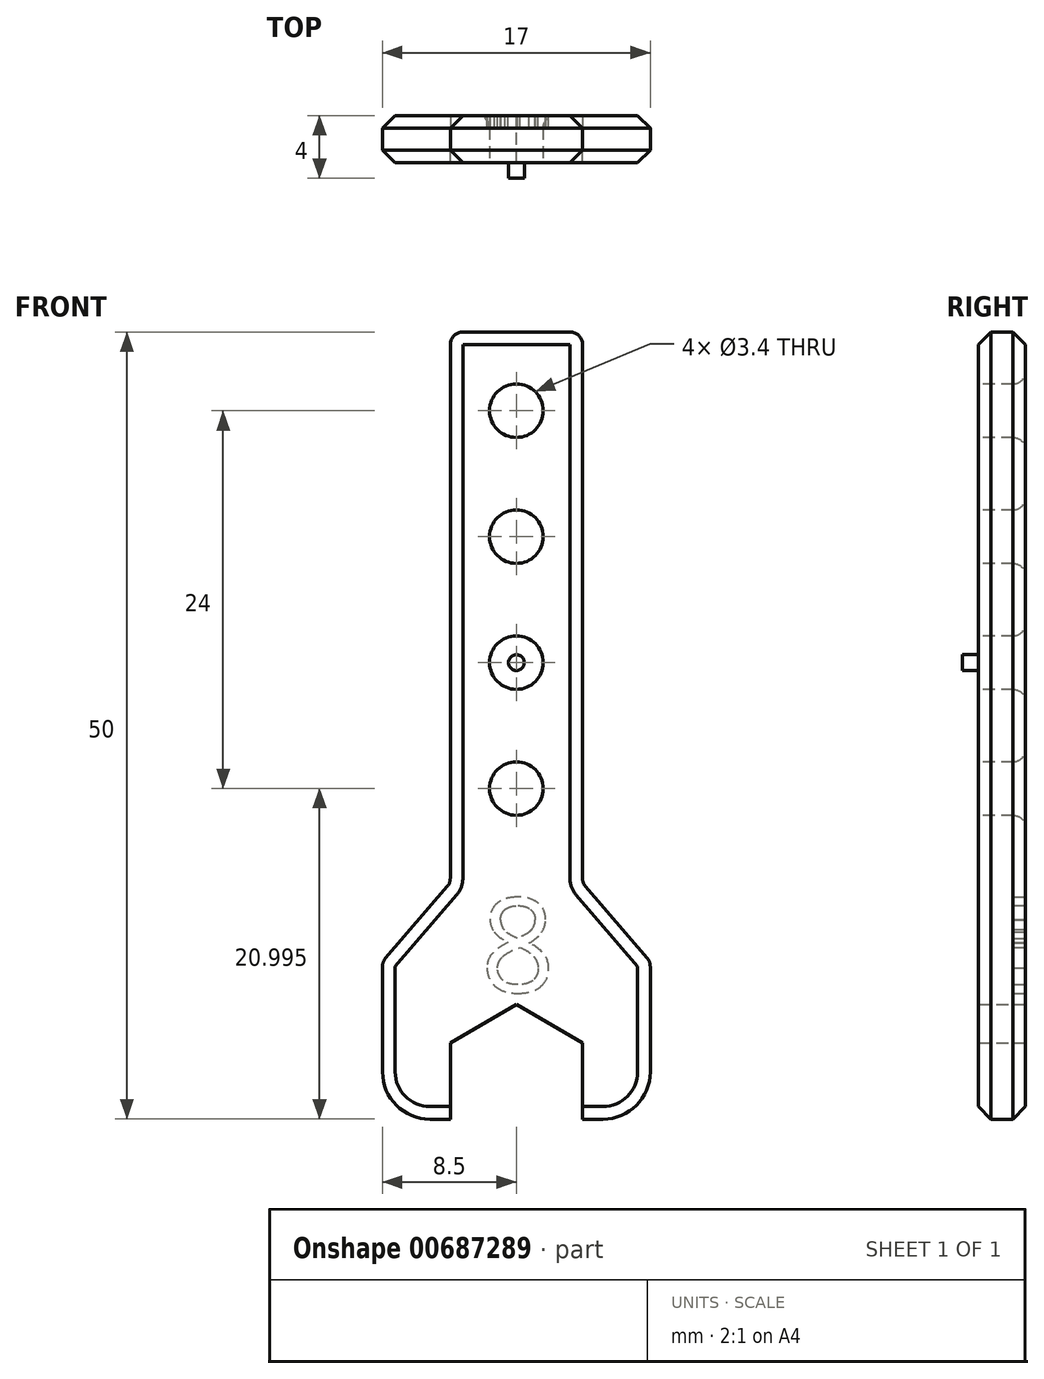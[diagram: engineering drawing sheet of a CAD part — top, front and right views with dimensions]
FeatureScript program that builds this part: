
annotation { "Feature Type Name" : "Feature", "Feature Type Description" : "" }
export const myFeature = defineFeature(function(context is Context, id is Id, definition is map)
    precondition{}
    {
        {
            var Q0;
            Q0=qCreatedBy(makeId("Front.planeOp"),FACE);
            var sketch = newSketch(context, id + "F0", { "sketchPlane" : qUnion([Q0])});
            skLineSegment(sketch, "E0.0", {"start": v(4.2, 2.42) * mm, "end": v(4.2, -2.42) * mm});
            skLineSegment(sketch, "E0.3", {"start": v(-4.2, -2.42) * mm, "end": v(-4.2, 2.42) * mm});
            skLineSegment(sketch, "E0.4", {"start": v(-4.2, 2.42) * mm, "end": v(0, 4.85) * mm});
            skLineSegment(sketch, "E0.5", {"start": v(0, 4.85) * mm, "end": v(2.1, 3.64) * mm});
            skPoint(sketch, "E0.0.midPoint", {"position": v(4.2, 0) * mm});
            skLineSegment(sketch, "E1", {"start": v(-8.5, -2.42) * mm, "end": v(-4.2, -2.42) * mm});
            skLineSegment(sketch, "E2", {"start": v(-8.5, -2.42) * mm, "end": v(-8.5, 7.58) * mm});
            skLineSegment(sketch, "E3", {"start": v(-8.5, 7.58) * mm, "end": v(-4.2, 12.58) * mm});
            skLineSegment(sketch, "E4", {"start": v(-4.2, 12.58) * mm, "end": v(-4.2, 47.58) * mm});
            skLineSegment(sketch, "E5", {"start": v(-4.2, 47.58) * mm, "end": v(0, 47.58) * mm});
            skLineSegment(sketch, "E6.MirrorCS", {"start": v(8.5, -2.42) * mm, "end": v(4.2, -2.42) * mm});
            skLineSegment(sketch, "E7.MirrorCS", {"start": v(4.2, 2.42) * mm, "end": v(0, 4.85) * mm});
            skLineSegment(sketch, "E8.MirrorCS", {"start": v(4.2, -2.42) * mm, "end": v(4.2, 2.42) * mm});
            skLineSegment(sketch, "E9.MirrorCS", {"start": v(4.2, 47.58) * mm, "end": v(0, 47.58) * mm});
            skLineSegment(sketch, "E10.MirrorCS", {"start": v(8.5, 7.58) * mm, "end": v(4.2, 12.58) * mm});
            skLineSegment(sketch, "E11.MirrorCS", {"start": v(8.5, -2.42) * mm, "end": v(8.5, 7.58) * mm});
            skLineSegment(sketch, "E12.MirrorCS", {"start": v(4.2, 12.58) * mm, "end": v(4.2, 47.58) * mm});
            skPoint(sketch, "E0.1.end.orphan", {"position": v(0, -4.85) * mm});
            skPoint(sketch, "E0.cCircle.center.orphan", {"position": v(0, 0) * mm});
            skSolve(sketch);
        }
        {
            var Q0;
            Q0=makeQuery(id+"F0.imprint","IMPRINT",FACE,{"disambiguationData":[TD([[makeQuery(id+"F0.imprint","IMPRINT",EDGE,{"derivedFrom":sQuery(id+"F0.wireOp",EDGE,"E0.3")}),1.0]])]});
            extrude(context, id + "F1", {"entities" : qUnion([Q0]), "endBound" : BoundingType.SYMMETRIC, "depth" : 3 * mm, "offsetDistance" : 25 * mm});
        }
        {
            var Q0;
            Q0=makeQuery(id+"F1.opExtrude","CAP_FACE",FACE,{"disambiguationData":[OSD([sQuery(id+"F0.wireOp",EDGE,"E0.3"),sQuery(id+"F0.wireOp",EDGE,"E0.4"),sQuery(id+"F0.wireOp",EDGE,"E1"),sQuery(id+"F0.wireOp",EDGE,"E2"),sQuery(id+"F0.wireOp",EDGE,"E3"),sQuery(id+"F0.wireOp",EDGE,"E4"),sQuery(id+"F0.wireOp",EDGE,"E5"),sQuery(id+"F0.wireOp",EDGE,"E6.MirrorCS"),sQuery(id+"F0.wireOp",EDGE,"E7.MirrorCS"),sQuery(id+"F0.wireOp",EDGE,"E8.MirrorCS"),sQuery(id+"F0.wireOp",EDGE,"E9.MirrorCS"),sQuery(id+"F0.wireOp",EDGE,"E10.MirrorCS"),sQuery(id+"F0.wireOp",EDGE,"E11.MirrorCS"),sQuery(id+"F0.wireOp",EDGE,"E12.MirrorCS")])],"isStart":false});
            var sketch = newSketch(context, id + "F2", { "sketchPlane" : qUnion([Q0])});
            skCircle(sketch, "E13", {"center": v(0, 42.58) * mm, "radius": 1.7 * mm});
            skCircle(sketch, "E14.0.1.0", {"center": v(0, 34.58) * mm, "radius": 1.7 * mm});
            skCircle(sketch, "E14.0.2.0", {"center": v(0, 26.58) * mm, "radius": 1.7 * mm});
            skCircle(sketch, "E14.0.3.0", {"center": v(0, 18.58) * mm, "radius": 1.7 * mm});
            skLineSegment(sketch, "E14.direction1", {"start": v(0, 42.58) * mm, "end": v(-27.7, 42.58) * mm, "construction": true});
            skLineSegment(sketch, "E14.direction2", {"start": v(0, 42.58) * mm, "end": v(0, 34.58) * mm, "construction": true});
            skSolve(sketch);
        }
        {
            var Q0;
            Q0 = qSketchRegion(id + "F2", true);
            extrude(context, id + "F3", {"entities" : qUnion([Q0]), "operationType" : NewBodyOperationType.REMOVE, "endBound" : BoundingType.THROUGH_ALL, "oppositeDirection" : true, "depth" : 25 * mm, "offsetDistance" : 25 * mm});
        }
        {
            var Q0;
            Q0=makeQuery(id+"F3.boolean.opBoolean","INTERSECT",EDGE,{"derivedFrom":[makeQuery(id+"F1.opExtrude","CAP_FACE",FACE,{"disambiguationData":[OSD([sQuery(id+"F0.wireOp",EDGE,"E0.3"),sQuery(id+"F0.wireOp",EDGE,"E0.4"),sQuery(id+"F0.wireOp",EDGE,"E1"),sQuery(id+"F0.wireOp",EDGE,"E2"),sQuery(id+"F0.wireOp",EDGE,"E3"),sQuery(id+"F0.wireOp",EDGE,"E4"),sQuery(id+"F0.wireOp",EDGE,"E5"),sQuery(id+"F0.wireOp",EDGE,"E6.MirrorCS"),sQuery(id+"F0.wireOp",EDGE,"E7.MirrorCS"),sQuery(id+"F0.wireOp",EDGE,"E8.MirrorCS"),sQuery(id+"F0.wireOp",EDGE,"E9.MirrorCS"),sQuery(id+"F0.wireOp",EDGE,"E10.MirrorCS"),sQuery(id+"F0.wireOp",EDGE,"E11.MirrorCS"),sQuery(id+"F0.wireOp",EDGE,"E12.MirrorCS")])],"isStart":true}),makeQuery(id+"F3.opExtrude","SWEPT_FACE",FACE,{"disambiguationData":[OSD([sQuery(id+"F2.wireOp",EDGE,"E14.0.4.0")])]})]});
            var Q1;
            Q1=makeQuery(id+"F3.boolean.opBoolean","INTERSECT",EDGE,{"derivedFrom":[makeQuery(id+"F1.opExtrude","CAP_FACE",FACE,{"disambiguationData":[OSD([sQuery(id+"F0.wireOp",EDGE,"E0.3"),sQuery(id+"F0.wireOp",EDGE,"E0.4"),sQuery(id+"F0.wireOp",EDGE,"E1"),sQuery(id+"F0.wireOp",EDGE,"E2"),sQuery(id+"F0.wireOp",EDGE,"E3"),sQuery(id+"F0.wireOp",EDGE,"E4"),sQuery(id+"F0.wireOp",EDGE,"E5"),sQuery(id+"F0.wireOp",EDGE,"E6.MirrorCS"),sQuery(id+"F0.wireOp",EDGE,"E7.MirrorCS"),sQuery(id+"F0.wireOp",EDGE,"E8.MirrorCS"),sQuery(id+"F0.wireOp",EDGE,"E9.MirrorCS"),sQuery(id+"F0.wireOp",EDGE,"E10.MirrorCS"),sQuery(id+"F0.wireOp",EDGE,"E11.MirrorCS"),sQuery(id+"F0.wireOp",EDGE,"E12.MirrorCS")])],"isStart":true}),makeQuery(id+"F3.opExtrude","SWEPT_FACE",FACE,{"disambiguationData":[OSD([sQuery(id+"F2.wireOp",EDGE,"E14.0.3.0")])]})]});
            var Q2;
            Q2=makeQuery(id+"F3.boolean.opBoolean","INTERSECT",EDGE,{"derivedFrom":[makeQuery(id+"F1.opExtrude","CAP_FACE",FACE,{"disambiguationData":[OSD([sQuery(id+"F0.wireOp",EDGE,"E0.3"),sQuery(id+"F0.wireOp",EDGE,"E0.4"),sQuery(id+"F0.wireOp",EDGE,"E1"),sQuery(id+"F0.wireOp",EDGE,"E2"),sQuery(id+"F0.wireOp",EDGE,"E3"),sQuery(id+"F0.wireOp",EDGE,"E4"),sQuery(id+"F0.wireOp",EDGE,"E5"),sQuery(id+"F0.wireOp",EDGE,"E6.MirrorCS"),sQuery(id+"F0.wireOp",EDGE,"E7.MirrorCS"),sQuery(id+"F0.wireOp",EDGE,"E8.MirrorCS"),sQuery(id+"F0.wireOp",EDGE,"E9.MirrorCS"),sQuery(id+"F0.wireOp",EDGE,"E10.MirrorCS"),sQuery(id+"F0.wireOp",EDGE,"E11.MirrorCS"),sQuery(id+"F0.wireOp",EDGE,"E12.MirrorCS")])],"isStart":true}),makeQuery(id+"F3.opExtrude","SWEPT_FACE",FACE,{"disambiguationData":[OSD([sQuery(id+"F2.wireOp",EDGE,"E13")])]})]});
            var Q3;
            Q3=makeQuery(id+"F3.boolean.opBoolean","INTERSECT",EDGE,{"derivedFrom":[makeQuery(id+"F1.opExtrude","CAP_FACE",FACE,{"disambiguationData":[OSD([sQuery(id+"F0.wireOp",EDGE,"E0.3"),sQuery(id+"F0.wireOp",EDGE,"E0.4"),sQuery(id+"F0.wireOp",EDGE,"E1"),sQuery(id+"F0.wireOp",EDGE,"E2"),sQuery(id+"F0.wireOp",EDGE,"E3"),sQuery(id+"F0.wireOp",EDGE,"E4"),sQuery(id+"F0.wireOp",EDGE,"E5"),sQuery(id+"F0.wireOp",EDGE,"E6.MirrorCS"),sQuery(id+"F0.wireOp",EDGE,"E7.MirrorCS"),sQuery(id+"F0.wireOp",EDGE,"E8.MirrorCS"),sQuery(id+"F0.wireOp",EDGE,"E9.MirrorCS"),sQuery(id+"F0.wireOp",EDGE,"E10.MirrorCS"),sQuery(id+"F0.wireOp",EDGE,"E11.MirrorCS"),sQuery(id+"F0.wireOp",EDGE,"E12.MirrorCS")])],"isStart":true}),makeQuery(id+"F3.opExtrude","SWEPT_FACE",FACE,{"disambiguationData":[OSD([sQuery(id+"F2.wireOp",EDGE,"E14.0.1.0")])]})]});
            var Q4;
            Q4=makeQuery(id+"F3.boolean.opBoolean","INTERSECT",EDGE,{"derivedFrom":[makeQuery(id+"F1.opExtrude","CAP_FACE",FACE,{"disambiguationData":[OSD([sQuery(id+"F0.wireOp",EDGE,"E0.3"),sQuery(id+"F0.wireOp",EDGE,"E0.4"),sQuery(id+"F0.wireOp",EDGE,"E1"),sQuery(id+"F0.wireOp",EDGE,"E2"),sQuery(id+"F0.wireOp",EDGE,"E3"),sQuery(id+"F0.wireOp",EDGE,"E4"),sQuery(id+"F0.wireOp",EDGE,"E5"),sQuery(id+"F0.wireOp",EDGE,"E6.MirrorCS"),sQuery(id+"F0.wireOp",EDGE,"E7.MirrorCS"),sQuery(id+"F0.wireOp",EDGE,"E8.MirrorCS"),sQuery(id+"F0.wireOp",EDGE,"E9.MirrorCS"),sQuery(id+"F0.wireOp",EDGE,"E10.MirrorCS"),sQuery(id+"F0.wireOp",EDGE,"E11.MirrorCS"),sQuery(id+"F0.wireOp",EDGE,"E12.MirrorCS")])],"isStart":true}),makeQuery(id+"F3.opExtrude","SWEPT_FACE",FACE,{"disambiguationData":[OSD([sQuery(id+"F2.wireOp",EDGE,"E14.0.2.0")])]})]});
            var Q5;
            Q5=makeQuery(id+"F3.boolean.opBoolean","COPY",EDGE,{"derivedFrom":makeQuery(id+"F3.opExtrude","CAP_EDGE",EDGE,{"disambiguationData":[OSD([sQuery(id+"F2.wireOp",EDGE,"E14.0.4.0")])],"isStart":true})});
            var Q6;
            Q6=makeQuery(id+"F3.boolean.opBoolean","COPY",EDGE,{"derivedFrom":makeQuery(id+"F3.opExtrude","CAP_EDGE",EDGE,{"disambiguationData":[OSD([sQuery(id+"F2.wireOp",EDGE,"E14.0.3.0")])],"isStart":true})});
            var Q7;
            Q7=makeQuery(id+"F3.boolean.opBoolean","COPY",EDGE,{"derivedFrom":makeQuery(id+"F3.opExtrude","CAP_EDGE",EDGE,{"disambiguationData":[OSD([sQuery(id+"F2.wireOp",EDGE,"E14.0.2.0")])],"isStart":true})});
            var Q8;
            Q8=makeQuery(id+"F3.boolean.opBoolean","COPY",EDGE,{"derivedFrom":makeQuery(id+"F3.opExtrude","CAP_EDGE",EDGE,{"disambiguationData":[OSD([sQuery(id+"F2.wireOp",EDGE,"E14.0.1.0")])],"isStart":true})});
            var Q9;
            Q9=makeQuery(id+"F3.boolean.opBoolean","COPY",EDGE,{"derivedFrom":makeQuery(id+"F3.opExtrude","CAP_EDGE",EDGE,{"disambiguationData":[OSD([sQuery(id+"F2.wireOp",EDGE,"E13")])],"isStart":true})});
            var Q10;
            Q10=makeQuery(id+"F1.opExtrude","SWEPT_EDGE",EDGE,{"disambiguationData":[OSD([sQuery(id+"F0.wireOp",EDGE,"E4"),sQuery(id+"F0.wireOp",EDGE,"E5")])]});
            var Q11;
            Q11=makeQuery(id+"F1.opExtrude","SWEPT_EDGE",EDGE,{"disambiguationData":[OSD([sQuery(id+"F0.wireOp",EDGE,"E9.MirrorCS"),sQuery(id+"F0.wireOp",EDGE,"E12.MirrorCS")])]});
            var Q12;
            Q12=makeQuery(id+"F1.opExtrude","SWEPT_EDGE",EDGE,{"disambiguationData":[OSD([sQuery(id+"F0.wireOp",EDGE,"E10.MirrorCS"),sQuery(id+"F0.wireOp",EDGE,"E11.MirrorCS")])]});
            var Q13;
            Q13=makeQuery(id+"F1.opExtrude","SWEPT_EDGE",EDGE,{"disambiguationData":[OSD([sQuery(id+"F0.wireOp",EDGE,"E3"),sQuery(id+"F0.wireOp",EDGE,"E4")])]});
            var Q14;
            Q14=makeQuery(id+"F1.opExtrude","SWEPT_EDGE",EDGE,{"disambiguationData":[OSD([sQuery(id+"F0.wireOp",EDGE,"E2"),sQuery(id+"F0.wireOp",EDGE,"E3")])]});
            var Q15;
            Q15=makeQuery(id+"F1.opExtrude","SWEPT_EDGE",EDGE,{"disambiguationData":[OSD([sQuery(id+"F0.wireOp",EDGE,"E10.MirrorCS"),sQuery(id+"F0.wireOp",EDGE,"E12.MirrorCS")])]});
            fillet(context, id + "F4", {"entities" : qUnion([Q0, Q1, Q2, Q3, Q4, Q5, Q6, Q7, Q8, Q9, Q10, Q11, Q12, Q13, Q14, Q15]), "radius" : 0.8 * mm, "tangentPropagation" : true, "allowEdgeOverflow" : false});
        }
        {
            var Q0;
            Q0=makeQuery(id+"F1.opExtrude","SWEPT_EDGE",EDGE,{"disambiguationData":[OSD([sQuery(id+"F0.wireOp",EDGE,"E1"),sQuery(id+"F0.wireOp",EDGE,"E2")])]});
            var Q1;
            Q1=makeQuery(id+"F1.opExtrude","SWEPT_EDGE",EDGE,{"disambiguationData":[OSD([sQuery(id+"F0.wireOp",EDGE,"E6.MirrorCS"),sQuery(id+"F0.wireOp",EDGE,"E11.MirrorCS")])]});
            fillet(context, id + "F5", {"entities" : qUnion([Q0, Q1]), "radius" : 3 * mm, "tangentPropagation" : true, "allowEdgeOverflow" : false});
        }
        {
            var Q0;
            Q0=makeQuery(id+"F1.opExtrude","CAP_EDGE",EDGE,{"disambiguationData":[OSD([sQuery(id+"F0.wireOp",EDGE,"E10.MirrorCS")])],"isStart":true});
            var Q1;
            Q1=makeQuery(id+"F1.opExtrude","CAP_EDGE",EDGE,{"disambiguationData":[OSD([sQuery(id+"F0.wireOp",EDGE,"E2")])],"isStart":false});
            chamfer(context, id + "F6", {"entities" : qUnion([Q0, Q1]), "width" : 0.8 * mm, "tangentPropagation" : true});
        }
        {
            var Q0;
            Q0=makeQuery(id+"F1.opExtrude","CAP_FACE",FACE,{"disambiguationData":[OSD([sQuery(id+"F0.wireOp",EDGE,"E0.3"),sQuery(id+"F0.wireOp",EDGE,"E0.4"),sQuery(id+"F0.wireOp",EDGE,"E1"),sQuery(id+"F0.wireOp",EDGE,"E2"),sQuery(id+"F0.wireOp",EDGE,"E3"),sQuery(id+"F0.wireOp",EDGE,"E4"),sQuery(id+"F0.wireOp",EDGE,"E5"),sQuery(id+"F0.wireOp",EDGE,"E6.MirrorCS"),sQuery(id+"F0.wireOp",EDGE,"E7.MirrorCS"),sQuery(id+"F0.wireOp",EDGE,"E8.MirrorCS"),sQuery(id+"F0.wireOp",EDGE,"E9.MirrorCS"),sQuery(id+"F0.wireOp",EDGE,"E10.MirrorCS"),sQuery(id+"F0.wireOp",EDGE,"E11.MirrorCS"),sQuery(id+"F0.wireOp",EDGE,"E12.MirrorCS")])],"isStart":true});
            var sketch = newSketch(context, id + "F7", { "sketchPlane" : qUnion([Q0])});
            skText(sketch, "E15", { "text": "8", "fontName": "OpenSans-Regular.ttf"});
            const initialGuessF7  = {"E15": [-0.00247, 0.00565, 1, 0, 0.006]};
            skSetInitialGuess(sketch, initialGuessF7);
            skSolve(sketch);
        }
        {
            var Q0;
            Q0 = qSketchRegion(id + "F7", true);
            extrude(context, id + "F8", {"entities" : qUnion([Q0]), "operationType" : NewBodyOperationType.REMOVE, "oppositeDirection" : true, "depth" : 0.8 * mm, "offsetDistance" : 25 * mm});
        }
        {
            var Q0;
            Q0=makeQuery(id+"F1.opExtrude","CAP_FACE",FACE,{"disambiguationData":[OSD([sQuery(id+"F0.wireOp",EDGE,"E0.3"),sQuery(id+"F0.wireOp",EDGE,"E0.4"),sQuery(id+"F0.wireOp",EDGE,"E1"),sQuery(id+"F0.wireOp",EDGE,"E2"),sQuery(id+"F0.wireOp",EDGE,"E3"),sQuery(id+"F0.wireOp",EDGE,"E4"),sQuery(id+"F0.wireOp",EDGE,"E5"),sQuery(id+"F0.wireOp",EDGE,"E6.MirrorCS"),sQuery(id+"F0.wireOp",EDGE,"E7.MirrorCS"),sQuery(id+"F0.wireOp",EDGE,"E8.MirrorCS"),sQuery(id+"F0.wireOp",EDGE,"E9.MirrorCS"),sQuery(id+"F0.wireOp",EDGE,"E10.MirrorCS"),sQuery(id+"F0.wireOp",EDGE,"E11.MirrorCS"),sQuery(id+"F0.wireOp",EDGE,"E12.MirrorCS")])],"isStart":false});
            var sketch = newSketch(context, id + "F9", { "sketchPlane" : qUnion([Q0])});
            skCircle(sketch, "E16", {"center": v(0, 26.58) * mm, "radius": 0.5 * mm});
            skSolve(sketch);
        }
        {
            var Q0;
            Q0 = qSketchRegion(id + "F9", true);
            extrude(context, id + "F10", {"entities" : qUnion([Q0]), "depth" : 1 * mm, "offsetDistance" : 25 * mm});
        }
    });
